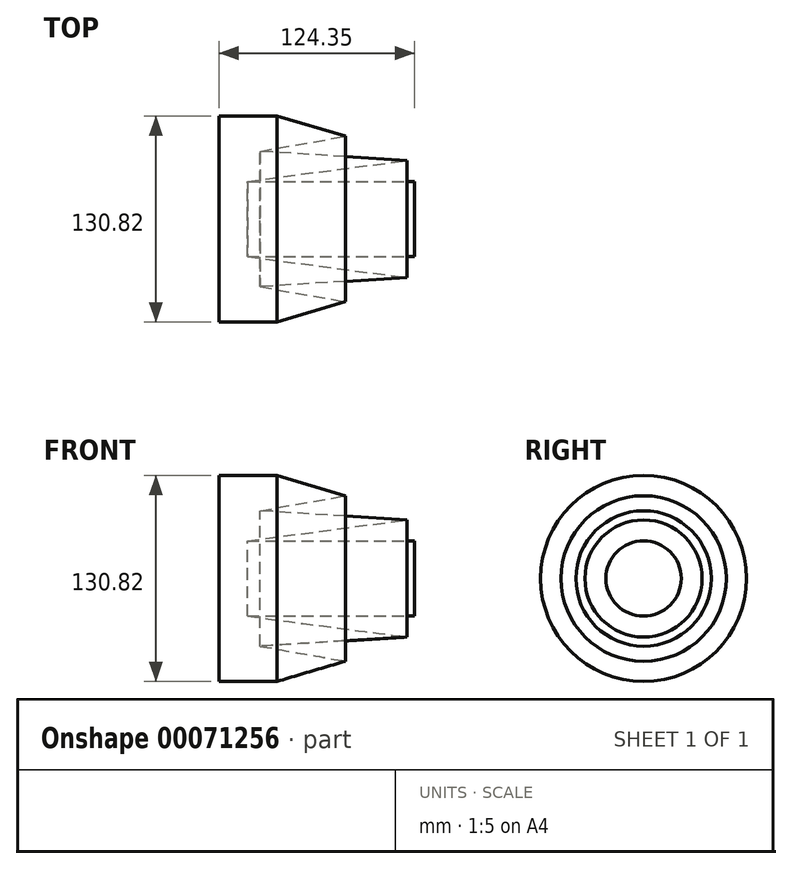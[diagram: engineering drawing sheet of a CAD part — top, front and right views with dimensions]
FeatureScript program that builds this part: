
annotation { "Feature Type Name" : "Feature", "Feature Type Description" : "" }
export const myFeature = defineFeature(function(context is Context, id is Id, definition is map)
    precondition{}
    {
        {
            var Q0;
            Q0=qCreatedBy(makeId("Top.planeOp"),FACE);
            var sketch = newSketch(context, id + "F0", { "sketchPlane" : qUnion([Q0])});
            skLineSegment(sketch, "E0", {"start": v(0, 0) * mm, "end": v(0, 65.4) * mm});
            skLineSegment(sketch, "E1", {"start": v(0, 65.4) * mm, "end": v(36.8, 65.4) * mm});
            skLineSegment(sketch, "E2", {"start": v(36.8, 65.4) * mm, "end": v(80.37, 52.55) * mm});
            skLineSegment(sketch, "E3", {"start": v(80.37, 52.55) * mm, "end": v(26.02, 43) * mm});
            skLineSegment(sketch, "E4", {"start": v(26.02, 43) * mm, "end": v(119.37, 37.2) * mm});
            skLineSegment(sketch, "E5", {"start": v(119.37, 37.2) * mm, "end": v(18.14, 23.92) * mm});
            skLineSegment(sketch, "E6", {"start": v(18.14, 23.92) * mm, "end": v(124.35, 23.92) * mm});
            skLineSegment(sketch, "E7", {"start": v(124.35, 23.92) * mm, "end": v(124.35, 0) * mm});
            skLineSegment(sketch, "E8", {"start": v(124.35, 0) * mm, "end": v(0, 0) * mm});
            skSolve(sketch);
        }
        {
            var Q0;
            Q0 = qSketchRegion(id + "F0", true);
            var Q1;
            Q1=sQuery(id+"F0.wireOp",EDGE,"E8");
            revolve(context, id + "F1", {"entities" : qUnion([Q0]), "axis" : qUnion([Q1]), "revolveType" : RevolveType.FULL});
        }
    });
